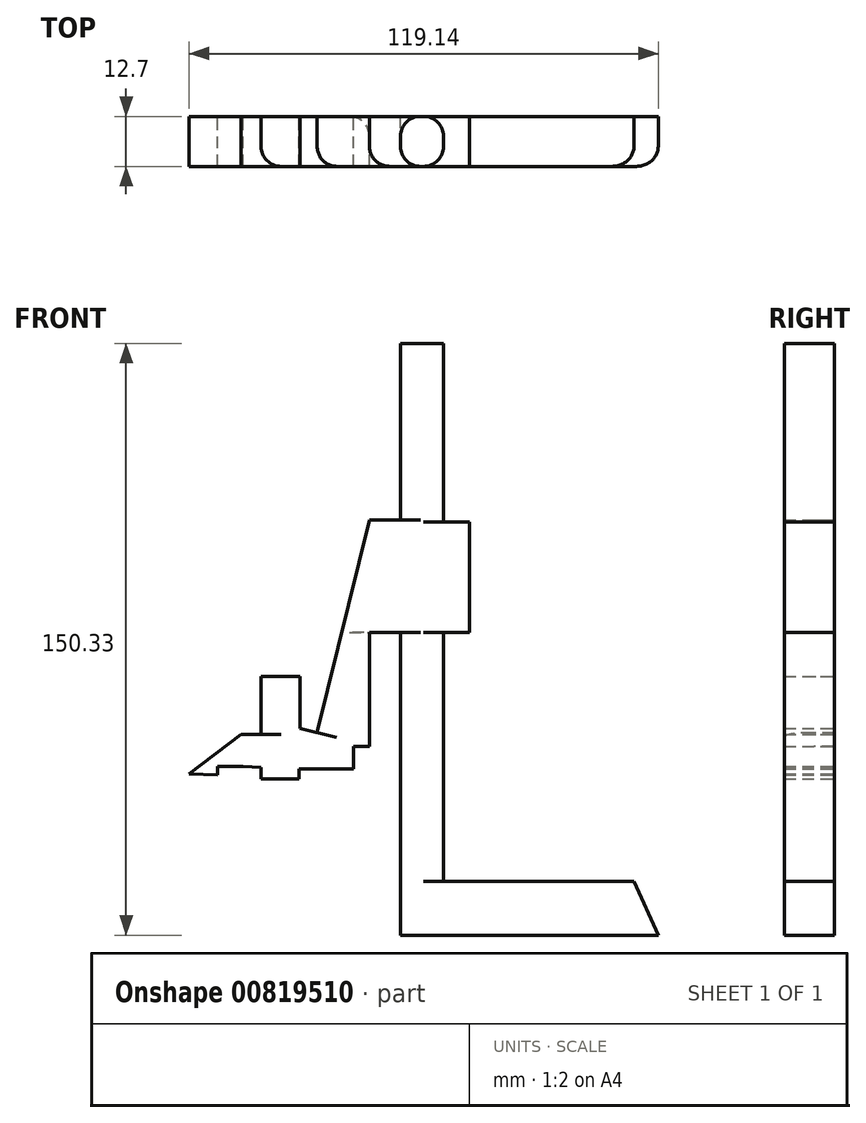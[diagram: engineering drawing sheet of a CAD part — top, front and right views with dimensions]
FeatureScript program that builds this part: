
annotation { "Feature Type Name" : "Feature", "Feature Type Description" : "" }
export const myFeature = defineFeature(function(context is Context, id is Id, definition is map)
    precondition{}
    {
        {
            var Q0;
            Q0=qCreatedBy(makeId("Front.planeOp"),FACE);
            var sketch = newSketch(context, id + "F0", { "sketchPlane" : qUnion([Q0])});
            skLineSegment(sketch, "E0.bottom", {"start": v(0, 73.38) * mm, "end": v(10.96, 73.38) * mm});
            skLineSegment(sketch, "E0.top", {"start": v(0, -76.95) * mm, "end": v(10.96, -76.95) * mm});
            skLineSegment(sketch, "E0.left", {"start": v(0, 73.38) * mm, "end": v(0, -76.95) * mm});
            skLineSegment(sketch, "E0.right", {"start": v(10.96, 73.38) * mm, "end": v(10.96, -76.95) * mm});
            skLineSegment(sketch, "E1.bottom", {"start": v(10.96, 28.03) * mm, "end": v(17.58, 28.03) * mm});
            skLineSegment(sketch, "E1.top", {"start": v(10.96, 0) * mm, "end": v(17.58, 0) * mm});
            skLineSegment(sketch, "E1.left", {"start": v(10.96, 28.03) * mm, "end": v(10.96, 0) * mm});
            skLineSegment(sketch, "E1.right", {"start": v(17.58, 28.03) * mm, "end": v(17.58, 0) * mm});
            skLineSegment(sketch, "E2.bottom", {"start": v(0, 28.54) * mm, "end": v(-7.9, 28.54) * mm});
            skLineSegment(sketch, "E2.top", {"start": v(0, 0) * mm, "end": v(-7.9, 0) * mm});
            skLineSegment(sketch, "E2.left", {"start": v(0, 28.54) * mm, "end": v(0, 0) * mm});
            skLineSegment(sketch, "E2.right", {"start": v(-7.9, 28.54) * mm, "end": v(-7.9, 0) * mm});
            skLineSegment(sketch, "E3.top", {"start": v(10.96, -76.95) * mm, "end": v(65.49, -76.95) * mm});
            skLineSegment(sketch, "E3.left", {"start": v(10.96, -57.59) * mm, "end": v(10.96, -76.95) * mm});
            skLineSegment(sketch, "E4", {"start": v(-7.9, 28.54) * mm, "end": v(-21.15, -25.48) * mm});
            skLineSegment(sketch, "E5", {"start": v(-21.15, -25.48) * mm, "end": v(-25.48, -24.42) * mm});
            skLineSegment(sketch, "E6", {"start": v(-25.48, -24.42) * mm, "end": v(-25.48, -11.21) * mm});
            skLineSegment(sketch, "E7", {"start": v(-25.48, -11.21) * mm, "end": v(-35.42, -11.21) * mm});
            skLineSegment(sketch, "E8", {"start": v(-35.42, -11.21) * mm, "end": v(-35.42, -26) * mm});
            skLineSegment(sketch, "E9", {"start": v(-35.42, -26) * mm, "end": v(-40.51, -26) * mm});
            skLineSegment(sketch, "E10", {"start": v(-7.9, 0) * mm, "end": v(-7.9, -29.05) * mm});
            skLineSegment(sketch, "E11", {"start": v(-7.9, -29.05) * mm, "end": v(-25.74, -29.05) * mm});
            skLineSegment(sketch, "E12", {"start": v(-25.74, -29.05) * mm, "end": v(-25.48, -24.42) * mm});
            skLineSegment(sketch, "E13", {"start": v(-11.91, -29.05) * mm, "end": v(-11.91, -34.75) * mm});
            skLineSegment(sketch, "E14", {"start": v(-11.91, -34.75) * mm, "end": v(-25.74, -34.75) * mm});
            skLineSegment(sketch, "E15", {"start": v(-25.74, -34.75) * mm, "end": v(-25.74, -37.32) * mm});
            skLineSegment(sketch, "E16", {"start": v(-25.74, -37.32) * mm, "end": v(-35.42, -37.32) * mm});
            skLineSegment(sketch, "E17", {"start": v(-35.42, -37.32) * mm, "end": v(-35.42, -34.32) * mm});
            skLineSegment(sketch, "E18", {"start": v(-35.42, -34.32) * mm, "end": v(-40, -34.14) * mm});
            skLineSegment(sketch, "E19", {"start": v(-40, -34.14) * mm, "end": v(-46.4, -34.14) * mm});
            skLineSegment(sketch, "E20", {"start": v(-46.4, -34.14) * mm, "end": v(-46.4, -36.25) * mm});
            skLineSegment(sketch, "E21", {"start": v(-46.4, -36.25) * mm, "end": v(-53.65, -35.97) * mm});
            skLineSegment(sketch, "E22", {"start": v(-40.51, -26) * mm, "end": v(-53.65, -35.97) * mm});
            skLineSegment(sketch, "E23", {"start": v(65.49, -76.95) * mm, "end": v(59.31, -63.25) * mm});
            skLineSegment(sketch, "E24", {"start": v(59.31, -63.25) * mm, "end": v(10.96, -63.25) * mm});
            skSolve(sketch);
        }
        {
            var Q0;
            Q0 = qSketchRegion(id + "F0", true);
            extrude(context, id + "F1", {"entities" : qUnion([Q0]), "depth" : 12.7 * mm, "offsetDistance" : 25.4 * mm});
        }
        {
            var Q0;
            Q0=makeQuery(id+"F1.opExtrude","CAP_EDGE",EDGE,{"disambiguationData":[OSD([sQuery(id+"F0.wireOp",EDGE,"E8")])],"isStart":false});
            var Q1;
            Q1=makeQuery(id+"F1.opExtrude","CAP_EDGE",EDGE,{"disambiguationData":[OSD([sQuery(id+"F0.wireOp",EDGE,"E0.right")])],"isStart":false});
            var Q2;
            Q2=makeQuery(id+"F1.opExtrude","CAP_EDGE",EDGE,{"disambiguationData":[OSD([sQuery(id+"F0.wireOp",EDGE,"E0.right")])],"isStart":true});
            var Q3;
            {var subQ0=sQuery(id+"F0.wireOp",EDGE,"E0.left");Q3=makeQuery(id+"F1.opExtrude","CAP_EDGE",EDGE,{"disambiguationData":[OSD([subQ0]),TDD([makeQuery(id+"F0.imprint","IMPRINT",EDGE,{"disambiguationData":[TD([[makeQuery(id+"F0.imprint","INTERSECT",VERTEX,{"derivedFrom":[sQuery(id+"F0.wireOp",EDGE,"E0.bottom"),subQ0]}),-1.0]])],"derivedFrom":subQ0})])],"isStart":false});}
            var Q4;
            Q4=makeQuery(id+"F1.opExtrude","CAP_EDGE",EDGE,{"disambiguationData":[OSD([sQuery(id+"F0.wireOp",EDGE,"E0.right"),sQuery(id+"F0.wireOp",EDGE,"E3.left")])],"isStart":false});
            var Q5;
            {var subQ0=sQuery(id+"F0.wireOp",EDGE,"E0.left");Q5=makeQuery(id+"F1.opExtrude","CAP_EDGE",EDGE,{"disambiguationData":[OSD([subQ0]),TDD([makeQuery(id+"F0.imprint","IMPRINT",EDGE,{"disambiguationData":[TD([[makeQuery(id+"F0.imprint","INTERSECT",VERTEX,{"derivedFrom":[sQuery(id+"F0.wireOp",EDGE,"E0.top"),subQ0]}),1.0]])],"derivedFrom":subQ0})])],"isStart":false});}
            fillet(context, id + "F2", {"entities" : qUnion([Q0, Q1, Q2, Q3, Q4, Q5]), "radius" : 5.08 * mm, "tangentPropagation" : true, "allowEdgeOverflow" : false});
        }
        {
            var Q0;
            Q0=makeQuery(id+"F1.opExtrude","CAP_EDGE",EDGE,{"disambiguationData":[OSD([sQuery(id+"F0.wireOp",EDGE,"E10")])],"isStart":true});
            var Q1;
            Q1=makeQuery(id+"F1.opExtrude","CAP_EDGE",EDGE,{"disambiguationData":[OSD([sQuery(id+"F0.wireOp",EDGE,"E4")])],"isStart":false});
            fillet(context, id + "F3", {"entities" : qUnion([Q0, Q1]), "radius" : 5.08 * mm, "tangentPropagation" : true, "allowEdgeOverflow" : false});
        }
        {
            var Q0;
            Q0=makeQuery(id+"F1.opExtrude","CAP_EDGE",EDGE,{"disambiguationData":[OSD([sQuery(id+"F0.wireOp",EDGE,"E23")])],"isStart":false});
            fillet(context, id + "F4", {"entities" : qUnion([Q0]), "radius" : 5.08 * mm, "tangentPropagation" : true, "allowEdgeOverflow" : false});
        }
        {
            var Q0;
            {var subQ0=sQuery(id+"F0.wireOp",EDGE,"E0.left");Q0=makeQuery(id+"F1.opExtrude","CAP_EDGE",EDGE,{"disambiguationData":[OSD([subQ0]),TDD([makeQuery(id+"F0.imprint","IMPRINT",EDGE,{"disambiguationData":[TD([[makeQuery(id+"F0.imprint","INTERSECT",VERTEX,{"derivedFrom":[sQuery(id+"F0.wireOp",EDGE,"E0.bottom"),subQ0]}),-1.0]])],"derivedFrom":subQ0})])],"isStart":true});}
            fillet(context, id + "F5", {"entities" : qUnion([Q0]), "radius" : 5.08 * mm, "tangentPropagation" : true, "allowEdgeOverflow" : false});
        }
    });
